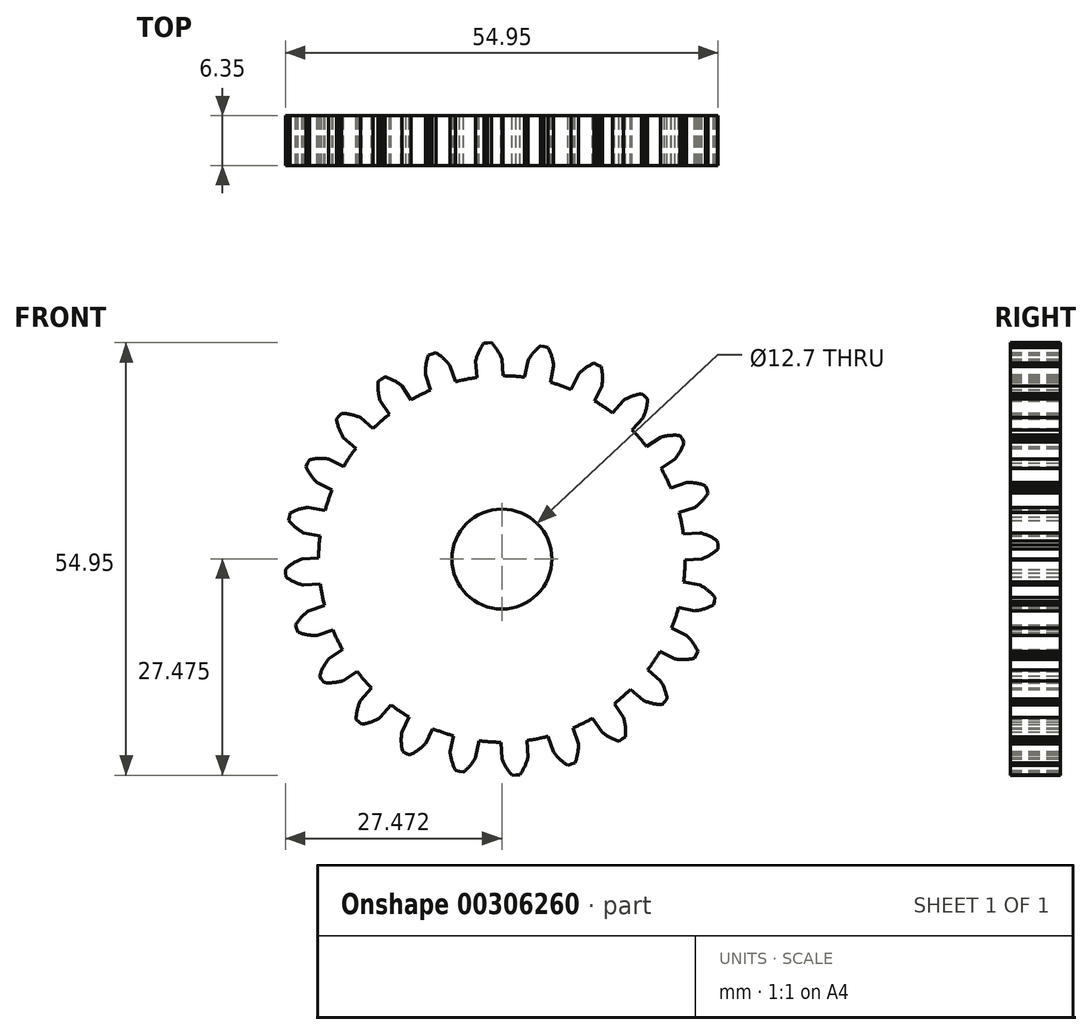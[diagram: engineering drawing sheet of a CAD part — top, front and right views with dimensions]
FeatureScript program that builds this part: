
annotation { "Feature Type Name" : "Feature", "Feature Type Description" : "" }
export const myFeature = defineFeature(function(context is Context, id is Id, definition is map)
    precondition{}
    {
        {
            var Q0;
            Q0=qCreatedBy(makeId("Front.planeOp"),FACE);
            var sketch = newSketch(context, id + "F0", { "sketchPlane" : qUnion([Q0])});
            skArc(sketch, "E0", {"start": v(-18.25, 13.05) * mm, "mid": v(-19.05, 11.92) * mm, "end": v(-19.79, 10.74) * mm});
            skArc(sketch, "E1", {"start": v(0.3, 24.38) * mm, "mid": v(-0.25, 25.49) * mm, "end": v(-1, 26.46) * mm});
            skLineSegment(sketch, "E2", {"start": v(0.3, 24.38) * mm, "end": v(0.44, 22.26) * mm});
            skLineSegment(sketch, "E3", {"start": v(-1, 26.46) * mm, "end": v(-1.5, 26.44) * mm});
            skLineSegment(sketch, "E4.MirrorCS", {"start": v(-1.99, 26.4) * mm, "end": v(-1.5, 26.44) * mm});
            skArc(sketch, "E5.MirrorCS", {"start": v(-3.01, 24.17) * mm, "mid": v(-2.6, 25.33) * mm, "end": v(-1.99, 26.4) * mm});
            skLineSegment(sketch, "E6.MirrorCS", {"start": v(-3.01, 24.17) * mm, "end": v(-2.87, 22.05) * mm});
            skPoint(sketch, "E7.orphan", {"position": v(-2.8, 20.9) * mm});
            skPoint(sketch, "E8.orphan", {"position": v(0.52, 21.11) * mm});
            skLineSegment(sketch, "E9.1.0", {"start": v(-9.42, 22.45) * mm, "end": v(-8.73, 20.44) * mm});
            skArc(sketch, "E9.1.1", {"start": v(-9.42, 22.45) * mm, "mid": v(-9.33, 23.68) * mm, "end": v(-9, 24.87) * mm});
            skLineSegment(sketch, "E9.1.2", {"start": v(-9, 24.87) * mm, "end": v(-8.54, 25.04) * mm});
            skLineSegment(sketch, "E9.1.3", {"start": v(-8.07, 25.19) * mm, "end": v(-8.54, 25.04) * mm});
            skArc(sketch, "E9.1.4", {"start": v(-6.27, 23.52) * mm, "mid": v(-7.1, 24.44) * mm, "end": v(-8.07, 25.19) * mm});
            skLineSegment(sketch, "E9.1.5", {"start": v(-6.27, 23.52) * mm, "end": v(-5.59, 21.5) * mm});
            skLineSegment(sketch, "E9.2.0", {"start": v(-15.16, 19.14) * mm, "end": v(-13.98, 17.37) * mm});
            skArc(sketch, "E9.2.1", {"start": v(-15.16, 19.14) * mm, "mid": v(-15.4, 20.35) * mm, "end": v(-15.39, 21.58) * mm});
            skLineSegment(sketch, "E9.2.2", {"start": v(-15.39, 21.58) * mm, "end": v(-14.98, 21.86) * mm});
            skLineSegment(sketch, "E9.2.3", {"start": v(-14.57, 22.13) * mm, "end": v(-14.98, 21.86) * mm});
            skArc(sketch, "E9.2.4", {"start": v(-12.4, 20.98) * mm, "mid": v(-13.43, 21.66) * mm, "end": v(-14.57, 22.13) * mm});
            skLineSegment(sketch, "E9.2.5", {"start": v(-12.4, 20.98) * mm, "end": v(-11.22, 19.21) * mm});
            skLineSegment(sketch, "E9.3.0", {"start": v(-19.85, 14.45) * mm, "end": v(-18.25, 13.05) * mm});
            skArc(sketch, "E9.3.1", {"start": v(-19.85, 14.45) * mm, "mid": v(-20.39, 15.56) * mm, "end": v(-20.7, 16.75) * mm});
            skLineSegment(sketch, "E9.3.2", {"start": v(-20.7, 16.75) * mm, "end": v(-20.38, 17.13) * mm});
            skLineSegment(sketch, "E9.3.3", {"start": v(-20.05, 17.5) * mm, "end": v(-20.38, 17.13) * mm});
            skArc(sketch, "E9.3.4", {"start": v(-17.66, 16.95) * mm, "mid": v(-18.83, 17.33) * mm, "end": v(-20.05, 17.5) * mm});
            skLineSegment(sketch, "E9.3.5", {"start": v(-17.66, 16.95) * mm, "end": v(-16.06, 15.54) * mm});
            skLineSegment(sketch, "E9.4.0", {"start": v(-23.16, 8.7) * mm, "end": v(-21.26, 7.76) * mm});
            skArc(sketch, "E9.4.1", {"start": v(-23.16, 8.7) * mm, "mid": v(-23.97, 9.64) * mm, "end": v(-24.58, 10.7) * mm});
            skLineSegment(sketch, "E9.4.2", {"start": v(-24.58, 10.7) * mm, "end": v(-24.37, 11.15) * mm});
            skLineSegment(sketch, "E9.4.3", {"start": v(-24.15, 11.6) * mm, "end": v(-24.37, 11.15) * mm});
            skArc(sketch, "E9.4.4", {"start": v(-21.7, 11.68) * mm, "mid": v(-22.93, 11.76) * mm, "end": v(-24.15, 11.6) * mm});
            skLineSegment(sketch, "E9.4.5", {"start": v(-21.7, 11.68) * mm, "end": v(-19.79, 10.74) * mm});
            skLineSegment(sketch, "E9.5.0", {"start": v(-24.88, 2.3) * mm, "end": v(-22.8, 1.89) * mm});
            skArc(sketch, "E9.5.1", {"start": v(-24.88, 2.3) * mm, "mid": v(-25.9, 3) * mm, "end": v(-26.77, 3.87) * mm});
            skLineSegment(sketch, "E9.5.2", {"start": v(-26.77, 3.87) * mm, "end": v(-26.68, 4.35) * mm});
            skLineSegment(sketch, "E9.5.3", {"start": v(-26.58, 4.83) * mm, "end": v(-26.68, 4.35) * mm});
            skArc(sketch, "E9.5.4", {"start": v(-24.23, 5.56) * mm, "mid": v(-25.44, 5.31) * mm, "end": v(-26.58, 4.83) * mm});
            skLineSegment(sketch, "E9.5.5", {"start": v(-24.23, 5.56) * mm, "end": v(-22.15, 5.14) * mm});
            skLineSegment(sketch, "E9.6.0", {"start": v(-24.88, -4.33) * mm, "end": v(-22.76, -4.2) * mm});
            skArc(sketch, "E9.6.1", {"start": v(-24.88, -4.33) * mm, "mid": v(-26.05, -3.93) * mm, "end": v(-27.11, -3.3) * mm});
            skLineSegment(sketch, "E9.6.2", {"start": v(-27.11, -3.3) * mm, "end": v(-27.15, -2.81) * mm});
            skLineSegment(sketch, "E9.6.3", {"start": v(-27.17, -2.32) * mm, "end": v(-27.15, -2.81) * mm});
            skArc(sketch, "E9.6.4", {"start": v(-25.1, -1.02) * mm, "mid": v(-26.2, -1.57) * mm, "end": v(-27.17, -2.32) * mm});
            skLineSegment(sketch, "E9.6.5", {"start": v(-25.1, -1.02) * mm, "end": v(-22.98, -0.88) * mm});
            skLineSegment(sketch, "E9.7.0", {"start": v(-23.16, -10.74) * mm, "end": v(-21.15, -10.05) * mm});
            skArc(sketch, "E9.7.1", {"start": v(-23.16, -10.74) * mm, "mid": v(-24.4, -10.65) * mm, "end": v(-25.58, -10.32) * mm});
            skLineSegment(sketch, "E9.7.2", {"start": v(-25.58, -10.32) * mm, "end": v(-25.75, -9.86) * mm});
            skLineSegment(sketch, "E9.7.3", {"start": v(-25.9, -9.39) * mm, "end": v(-25.75, -9.86) * mm});
            skArc(sketch, "E9.7.4", {"start": v(-24.23, -7.59) * mm, "mid": v(-25.15, -8.4) * mm, "end": v(-25.9, -9.39) * mm});
            skLineSegment(sketch, "E9.7.5", {"start": v(-24.23, -7.59) * mm, "end": v(-22.22, -6.9) * mm});
            skLineSegment(sketch, "E9.8.0", {"start": v(-19.85, -16.48) * mm, "end": v(-18.08, -15.3) * mm});
            skArc(sketch, "E9.8.1", {"start": v(-19.85, -16.48) * mm, "mid": v(-21.06, -16.71) * mm, "end": v(-22.3, -16.7) * mm});
            skLineSegment(sketch, "E9.8.2", {"start": v(-22.3, -16.7) * mm, "end": v(-22.57, -16.3) * mm});
            skLineSegment(sketch, "E9.8.3", {"start": v(-22.84, -15.89) * mm, "end": v(-22.57, -16.3) * mm});
            skArc(sketch, "E9.8.4", {"start": v(-21.7, -13.72) * mm, "mid": v(-22.37, -14.74) * mm, "end": v(-22.84, -15.89) * mm});
            skLineSegment(sketch, "E9.8.5", {"start": v(-21.7, -13.72) * mm, "end": v(-19.93, -12.53) * mm});
            skLineSegment(sketch, "E9.9.0", {"start": v(-15.16, -21.17) * mm, "end": v(-13.76, -19.57) * mm});
            skArc(sketch, "E9.9.1", {"start": v(-15.16, -21.17) * mm, "mid": v(-16.27, -21.7) * mm, "end": v(-17.46, -22.02) * mm});
            skLineSegment(sketch, "E9.9.2", {"start": v(-17.46, -22.02) * mm, "end": v(-17.84, -21.7) * mm});
            skLineSegment(sketch, "E9.9.3", {"start": v(-18.2, -21.37) * mm, "end": v(-17.84, -21.7) * mm});
            skArc(sketch, "E9.9.4", {"start": v(-17.66, -18.98) * mm, "mid": v(-18.05, -20.15) * mm, "end": v(-18.2, -21.37) * mm});
            skLineSegment(sketch, "E9.9.5", {"start": v(-17.66, -18.98) * mm, "end": v(-16.26, -17.38) * mm});
            skLineSegment(sketch, "E9.10.0", {"start": v(-9.42, -24.48) * mm, "end": v(-8.48, -22.57) * mm});
            skArc(sketch, "E9.10.1", {"start": v(-9.42, -24.48) * mm, "mid": v(-10.35, -25.29) * mm, "end": v(-11.42, -25.9) * mm});
            skLineSegment(sketch, "E9.10.2", {"start": v(-11.42, -25.9) * mm, "end": v(-11.87, -25.7) * mm});
            skLineSegment(sketch, "E9.10.3", {"start": v(-12.3, -25.46) * mm, "end": v(-11.87, -25.7) * mm});
            skArc(sketch, "E9.10.4", {"start": v(-12.4, -23.01) * mm, "mid": v(-12.47, -24.24) * mm, "end": v(-12.3, -25.46) * mm});
            skLineSegment(sketch, "E9.10.5", {"start": v(-12.4, -23.01) * mm, "end": v(-11.46, -21.1) * mm});
            skLineSegment(sketch, "E9.11.0", {"start": v(-3.01, -26.2) * mm, "end": v(-2.6, -24.11) * mm});
            skArc(sketch, "E9.11.1", {"start": v(-3.01, -26.2) * mm, "mid": v(-3.7, -27.22) * mm, "end": v(-4.58, -28.09) * mm});
            skLineSegment(sketch, "E9.11.2", {"start": v(-4.58, -28.09) * mm, "end": v(-5.07, -28) * mm});
            skLineSegment(sketch, "E9.11.3", {"start": v(-5.55, -27.9) * mm, "end": v(-5.07, -28) * mm});
            skArc(sketch, "E9.11.4", {"start": v(-6.27, -25.55) * mm, "mid": v(-6.02, -26.76) * mm, "end": v(-5.55, -27.9) * mm});
            skLineSegment(sketch, "E9.11.5", {"start": v(-6.27, -25.55) * mm, "end": v(-5.86, -23.46) * mm});
            skLineSegment(sketch, "E9.12.0", {"start": v(3.62, -26.2) * mm, "end": v(3.48, -24.08) * mm});
            skArc(sketch, "E9.12.1", {"start": v(3.62, -26.2) * mm, "mid": v(3.21, -27.36) * mm, "end": v(2.6, -28.43) * mm});
            skLineSegment(sketch, "E9.12.2", {"start": v(2.6, -28.43) * mm, "end": v(2.1, -28.47) * mm});
            skLineSegment(sketch, "E9.12.3", {"start": v(1.6, -28.5) * mm, "end": v(2.1, -28.47) * mm});
            skArc(sketch, "E9.12.4", {"start": v(0.3, -26.42) * mm, "mid": v(0.85, -27.52) * mm, "end": v(1.6, -28.5) * mm});
            skLineSegment(sketch, "E9.12.5", {"start": v(0.3, -26.42) * mm, "end": v(0.16, -24.3) * mm});
            skLineSegment(sketch, "E9.13.0", {"start": v(10.02, -24.48) * mm, "end": v(9.34, -22.47) * mm});
            skArc(sketch, "E9.13.1", {"start": v(10.02, -24.48) * mm, "mid": v(9.93, -25.71) * mm, "end": v(9.6, -26.9) * mm});
            skLineSegment(sketch, "E9.13.2", {"start": v(9.6, -26.9) * mm, "end": v(9.15, -27.07) * mm});
            skLineSegment(sketch, "E9.13.3", {"start": v(8.68, -27.22) * mm, "end": v(9.15, -27.07) * mm});
            skArc(sketch, "E9.13.4", {"start": v(6.88, -25.55) * mm, "mid": v(7.7, -26.47) * mm, "end": v(8.68, -27.22) * mm});
            skLineSegment(sketch, "E9.13.5", {"start": v(6.88, -25.55) * mm, "end": v(6.2, -23.54) * mm});
            skLineSegment(sketch, "E9.14.0", {"start": v(15.76, -21.17) * mm, "end": v(14.58, -19.4) * mm});
            skArc(sketch, "E9.14.1", {"start": v(15.76, -21.17) * mm, "mid": v(16, -22.38) * mm, "end": v(16, -23.6) * mm});
            skLineSegment(sketch, "E9.14.2", {"start": v(16, -23.6) * mm, "end": v(15.59, -23.9) * mm});
            skLineSegment(sketch, "E9.14.3", {"start": v(15.17, -24.16) * mm, "end": v(15.59, -23.9) * mm});
            skArc(sketch, "E9.14.4", {"start": v(13, -23.01) * mm, "mid": v(14.03, -23.7) * mm, "end": v(15.17, -24.16) * mm});
            skLineSegment(sketch, "E9.14.5", {"start": v(13, -23.01) * mm, "end": v(11.82, -21.24) * mm});
            skLineSegment(sketch, "E9.15.0", {"start": v(20.45, -16.48) * mm, "end": v(18.86, -15.08) * mm});
            skArc(sketch, "E9.15.1", {"start": v(20.45, -16.48) * mm, "mid": v(21, -17.59) * mm, "end": v(21.3, -18.78) * mm});
            skLineSegment(sketch, "E9.15.2", {"start": v(21.3, -18.78) * mm, "end": v(20.99, -19.16) * mm});
            skLineSegment(sketch, "E9.15.3", {"start": v(20.66, -19.52) * mm, "end": v(20.99, -19.16) * mm});
            skArc(sketch, "E9.15.4", {"start": v(18.26, -18.98) * mm, "mid": v(19.43, -19.36) * mm, "end": v(20.66, -19.52) * mm});
            skLineSegment(sketch, "E9.15.5", {"start": v(18.26, -18.98) * mm, "end": v(16.66, -17.57) * mm});
            skLineSegment(sketch, "E9.16.0", {"start": v(23.77, -10.74) * mm, "end": v(21.86, -9.8) * mm});
            skArc(sketch, "E9.16.1", {"start": v(23.77, -10.74) * mm, "mid": v(24.58, -11.67) * mm, "end": v(25.19, -12.74) * mm});
            skLineSegment(sketch, "E9.16.2", {"start": v(25.19, -12.74) * mm, "end": v(24.98, -13.18) * mm});
            skLineSegment(sketch, "E9.16.3", {"start": v(24.75, -13.62) * mm, "end": v(24.98, -13.18) * mm});
            skArc(sketch, "E9.16.4", {"start": v(22.3, -13.72) * mm, "mid": v(23.53, -13.79) * mm, "end": v(24.75, -13.62) * mm});
            skLineSegment(sketch, "E9.16.5", {"start": v(22.3, -13.72) * mm, "end": v(20.4, -12.77) * mm});
            skLineSegment(sketch, "E9.17.0", {"start": v(25.49, -4.33) * mm, "end": v(23.4, -3.92) * mm});
            skArc(sketch, "E9.17.1", {"start": v(25.49, -4.33) * mm, "mid": v(26.5, -5.02) * mm, "end": v(27.37, -5.9) * mm});
            skLineSegment(sketch, "E9.17.2", {"start": v(27.37, -5.9) * mm, "end": v(27.29, -6.38) * mm});
            skLineSegment(sketch, "E9.17.3", {"start": v(27.18, -6.86) * mm, "end": v(27.29, -6.38) * mm});
            skArc(sketch, "E9.17.4", {"start": v(24.84, -7.59) * mm, "mid": v(26.04, -7.34) * mm, "end": v(27.18, -6.86) * mm});
            skLineSegment(sketch, "E9.17.5", {"start": v(24.84, -7.59) * mm, "end": v(22.75, -7.17) * mm});
            skLineSegment(sketch, "E9.18.0", {"start": v(25.49, 2.3) * mm, "end": v(23.36, 2.16) * mm});
            skArc(sketch, "E9.18.1", {"start": v(25.49, 2.3) * mm, "mid": v(26.65, 1.9) * mm, "end": v(27.71, 1.28) * mm});
            skLineSegment(sketch, "E9.18.2", {"start": v(27.71, 1.28) * mm, "end": v(27.76, 0.78) * mm});
            skLineSegment(sketch, "E9.18.3", {"start": v(27.78, 0.3) * mm, "end": v(27.76, 0.78) * mm});
            skArc(sketch, "E9.18.4", {"start": v(25.7, -1.02) * mm, "mid": v(26.8, -0.46) * mm, "end": v(27.78, 0.3) * mm});
            skLineSegment(sketch, "E9.18.5", {"start": v(25.7, -1.02) * mm, "end": v(23.58, -1.15) * mm});
            skLineSegment(sketch, "E9.19.0", {"start": v(23.77, 8.7) * mm, "end": v(21.76, 8.02) * mm});
            skArc(sketch, "E9.19.1", {"start": v(23.77, 8.7) * mm, "mid": v(25, 8.62) * mm, "end": v(26.19, 8.3) * mm});
            skLineSegment(sketch, "E9.19.2", {"start": v(26.19, 8.3) * mm, "end": v(26.35, 7.83) * mm});
            skLineSegment(sketch, "E9.19.3", {"start": v(26.5, 7.36) * mm, "end": v(26.35, 7.83) * mm});
            skArc(sketch, "E9.19.4", {"start": v(24.84, 5.56) * mm, "mid": v(25.76, 6.38) * mm, "end": v(26.5, 7.36) * mm});
            skLineSegment(sketch, "E9.19.5", {"start": v(24.84, 5.56) * mm, "end": v(22.82, 4.88) * mm});
            skLineSegment(sketch, "E9.20.0", {"start": v(20.45, 14.45) * mm, "end": v(18.69, 13.27) * mm});
            skArc(sketch, "E9.20.1", {"start": v(20.45, 14.45) * mm, "mid": v(21.66, 14.68) * mm, "end": v(22.9, 14.68) * mm});
            skLineSegment(sketch, "E9.20.2", {"start": v(22.9, 14.68) * mm, "end": v(23.18, 14.27) * mm});
            skLineSegment(sketch, "E9.20.3", {"start": v(23.44, 13.86) * mm, "end": v(23.18, 14.27) * mm});
            skArc(sketch, "E9.20.4", {"start": v(22.3, 11.68) * mm, "mid": v(22.98, 12.71) * mm, "end": v(23.44, 13.86) * mm});
            skLineSegment(sketch, "E9.20.5", {"start": v(22.3, 11.68) * mm, "end": v(20.53, 10.5) * mm});
            skLineSegment(sketch, "E9.21.0", {"start": v(15.76, 19.14) * mm, "end": v(14.36, 17.54) * mm});
            skArc(sketch, "E9.21.1", {"start": v(15.76, 19.14) * mm, "mid": v(16.87, 19.67) * mm, "end": v(18.07, 19.99) * mm});
            skLineSegment(sketch, "E9.21.2", {"start": v(18.07, 19.99) * mm, "end": v(18.44, 19.67) * mm});
            skLineSegment(sketch, "E9.21.3", {"start": v(18.8, 19.34) * mm, "end": v(18.44, 19.67) * mm});
            skArc(sketch, "E9.21.4", {"start": v(18.26, 16.95) * mm, "mid": v(18.65, 18.12) * mm, "end": v(18.8, 19.34) * mm});
            skLineSegment(sketch, "E9.21.5", {"start": v(18.26, 16.95) * mm, "end": v(16.86, 15.35) * mm});
            skLineSegment(sketch, "E9.22.0", {"start": v(10.02, 22.45) * mm, "end": v(9.08, 20.54) * mm});
            skArc(sketch, "E9.22.1", {"start": v(10.02, 22.45) * mm, "mid": v(10.95, 23.26) * mm, "end": v(12.02, 23.87) * mm});
            skLineSegment(sketch, "E9.22.2", {"start": v(12.02, 23.87) * mm, "end": v(12.47, 23.66) * mm});
            skLineSegment(sketch, "E9.22.3", {"start": v(12.9, 23.43) * mm, "end": v(12.47, 23.66) * mm});
            skArc(sketch, "E9.22.4", {"start": v(13, 20.98) * mm, "mid": v(13.08, 22.21) * mm, "end": v(12.9, 23.43) * mm});
            skLineSegment(sketch, "E9.22.5", {"start": v(13, 20.98) * mm, "end": v(12.06, 19.08) * mm});
            skLineSegment(sketch, "E9.23.0", {"start": v(3.62, 24.17) * mm, "end": v(3.2, 22.08) * mm});
            skArc(sketch, "E9.23.1", {"start": v(3.62, 24.17) * mm, "mid": v(4.3, 25.19) * mm, "end": v(5.18, 26.06) * mm});
            skLineSegment(sketch, "E9.23.2", {"start": v(5.18, 26.06) * mm, "end": v(5.67, 25.97) * mm});
            skLineSegment(sketch, "E9.23.3", {"start": v(6.15, 25.86) * mm, "end": v(5.67, 25.97) * mm});
            skArc(sketch, "E9.23.4", {"start": v(6.88, 23.52) * mm, "mid": v(6.63, 24.73) * mm, "end": v(6.15, 25.86) * mm});
            skLineSegment(sketch, "E9.23.5", {"start": v(6.88, 23.52) * mm, "end": v(6.46, 21.43) * mm});
            skArc(sketch, "E10.trimOffspring", {"start": v(-13.98, 17.37) * mm, "mid": v(-15.05, 16.49) * mm, "end": v(-16.06, 15.54) * mm});
            skArc(sketch, "E11.trimOffspring", {"start": v(-8.73, 20.44) * mm, "mid": v(-10, 19.86) * mm, "end": v(-11.22, 19.21) * mm});
            skArc(sketch, "E12.trimOffspring", {"start": v(-2.87, 22.05) * mm, "mid": v(-4.24, 21.82) * mm, "end": v(-5.59, 21.5) * mm});
            skArc(sketch, "E13.trimOffspring", {"start": v(3.2, 22.08) * mm, "mid": v(1.82, 22.21) * mm, "end": v(0.44, 22.26) * mm});
            skArc(sketch, "E14.trimOffspring", {"start": v(9.08, 20.54) * mm, "mid": v(7.79, 21.03) * mm, "end": v(6.46, 21.43) * mm});
            skArc(sketch, "E15.trimOffspring", {"start": v(14.36, 17.54) * mm, "mid": v(13.24, 18.34) * mm, "end": v(12.06, 19.08) * mm});
            skArc(sketch, "E16.trimOffspring", {"start": v(18.69, 13.27) * mm, "mid": v(17.8, 14.33) * mm, "end": v(16.86, 15.35) * mm});
            skArc(sketch, "E17.trimOffspring", {"start": v(21.76, 8.02) * mm, "mid": v(21.18, 9.28) * mm, "end": v(20.53, 10.5) * mm});
            skArc(sketch, "E18.trimOffspring", {"start": v(23.36, 2.16) * mm, "mid": v(23.13, 3.53) * mm, "end": v(22.82, 4.88) * mm});
            skArc(sketch, "E19.trimOffspring", {"start": v(23.4, -3.92) * mm, "mid": v(23.53, -2.54) * mm, "end": v(23.58, -1.15) * mm});
            skArc(sketch, "E20.trimOffspring", {"start": v(21.86, -9.8) * mm, "mid": v(22.35, -8.5) * mm, "end": v(22.75, -7.17) * mm});
            skArc(sketch, "E21.trimOffspring", {"start": v(18.86, -15.08) * mm, "mid": v(19.66, -13.95) * mm, "end": v(20.4, -12.77) * mm});
            skArc(sketch, "E22.trimOffspring", {"start": v(14.58, -19.4) * mm, "mid": v(15.65, -18.52) * mm, "end": v(16.66, -17.57) * mm});
            skArc(sketch, "E23.trimOffspring", {"start": v(9.34, -22.47) * mm, "mid": v(10.6, -21.9) * mm, "end": v(11.82, -21.24) * mm});
            skArc(sketch, "E24.trimOffspring", {"start": v(3.48, -24.08) * mm, "mid": v(4.84, -23.85) * mm, "end": v(6.2, -23.54) * mm});
            skArc(sketch, "E25.trimOffspring", {"start": v(-2.6, -24.11) * mm, "mid": v(-1.22, -24.24) * mm, "end": v(0.16, -24.3) * mm});
            skArc(sketch, "E26.trimOffspring", {"start": v(-8.48, -22.57) * mm, "mid": v(-7.18, -23.06) * mm, "end": v(-5.86, -23.46) * mm});
            skArc(sketch, "E27.trimOffspring", {"start": v(-13.76, -19.57) * mm, "mid": v(-12.63, -20.37) * mm, "end": v(-11.46, -21.1) * mm});
            skArc(sketch, "E28.trimOffspring", {"start": v(-18.08, -15.3) * mm, "mid": v(-17.2, -16.36) * mm, "end": v(-16.26, -17.38) * mm});
            skArc(sketch, "E29.trimOffspring", {"start": v(-21.15, -10.05) * mm, "mid": v(-20.58, -11.31) * mm, "end": v(-19.93, -12.53) * mm});
            skArc(sketch, "E30.trimOffspring", {"start": v(-22.76, -4.2) * mm, "mid": v(-22.53, -5.56) * mm, "end": v(-22.22, -6.9) * mm});
            skArc(sketch, "E31.trimOffspring", {"start": v(-22.8, 1.89) * mm, "mid": v(-22.93, 0.5) * mm, "end": v(-22.98, -0.88) * mm});
            skArc(sketch, "E32.trimOffspring", {"start": v(-21.26, 7.76) * mm, "mid": v(-21.74, 6.47) * mm, "end": v(-22.15, 5.14) * mm});
            skCircle(sketch, "E33", {"center": v(0.3, -1.02) * mm, "radius": 6.35 * mm});
            skSolve(sketch);
        }
        {
            var Q0;
            Q0 = qSketchRegion(id + "F0", true);
            extrude(context, id + "F1", {"entities" : qUnion([Q0]), "depth" : 6.35 * mm});
        }
    });
